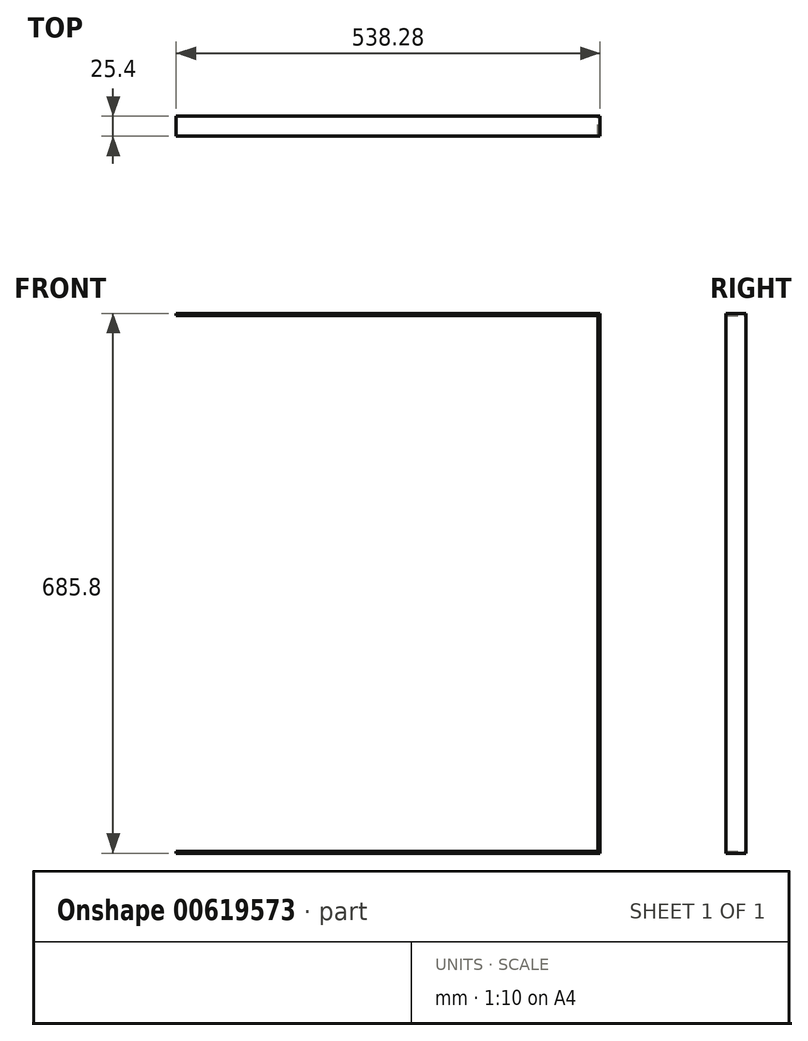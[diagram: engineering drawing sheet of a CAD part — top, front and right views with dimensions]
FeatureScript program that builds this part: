
annotation { "Feature Type Name" : "Feature", "Feature Type Description" : "" }
export const myFeature = defineFeature(function(context is Context, id is Id, definition is map)
    precondition{}
    {
        {
            var Q0;
            Q0=qCreatedBy(makeId("Front.planeOp"),FACE);
            var sketch = newSketch(context, id + "F0", { "sketchPlane" : qUnion([Q0])});
            skLineSegment(sketch, "E0.bottom", {"start": v(-568.3, 468.03) * mm, "end": v(549.3, 468.03) * mm});
            skLineSegment(sketch, "E0.top", {"start": v(-568.3, -217.77) * mm, "end": v(549.3, -217.77) * mm});
            skLineSegment(sketch, "E0.left", {"start": v(-568.3, 468.03) * mm, "end": v(-568.3, -217.77) * mm});
            skLineSegment(sketch, "E0.right", {"start": v(549.3, 468.03) * mm, "end": v(549.3, -217.77) * mm});
            skLineSegment(sketch, "E1", {"start": v(-568.3, 468.03) * mm, "end": v(-555.39, 468.03) * mm});
            skLineSegment(sketch, "E2", {"start": v(-555.39, 468.03) * mm, "end": v(-555.39, -217.77) * mm});
            skLineSegment(sketch, "E3.1.0.0", {"start": v(-4.2, 468.03) * mm, "end": v(-4.2, -217.77) * mm});
            skLineSegment(sketch, "E3.1.0.1", {"start": v(-17.11, 468.03) * mm, "end": v(-4.2, 468.03) * mm});
            skLineSegment(sketch, "E3.1.0.2", {"start": v(-17.11, 468.03) * mm, "end": v(-17.11, -217.77) * mm});
            skLineSegment(sketch, "E3.2.0.0", {"start": v(546.97, 468.03) * mm, "end": v(546.97, -217.77) * mm});
            skLineSegment(sketch, "E3.2.0.1", {"start": v(534.07, 468.03) * mm, "end": v(546.97, 468.03) * mm});
            skLineSegment(sketch, "E3.2.0.2", {"start": v(534.07, 468.03) * mm, "end": v(534.07, -217.77) * mm});
            skLineSegment(sketch, "E3.direction1", {"start": v(-555.39, -217.77) * mm, "end": v(-4.2, -217.77) * mm, "construction": true});
            skSolve(sketch);
        }
        {
            var Q0;
            {var subQ0=sQuery(id+"F0.wireOp",EDGE,"E2");Q0=makeQuery(id+"F0.imprint","IMPRINT",FACE,{"disambiguationData":[TD([[makeQuery(id+"F0.imprint","IMPRINT",EDGE,{"derivedFrom":subQ0}),1.0]])]});}
            extrude(context, id + "F1", {"entities" : qUnion([Q0]), "depth" : 25.4 * mm, "offsetDistance" : 25.4 * mm});
        }
        {
            var Q0;
            Q0=makeQuery(id+"F1.opExtrude","SWEPT_FACE",FACE,{"disambiguationData":[OSD([sQuery(id+"F0.wireOp",EDGE,"E2")])]});
            var Q1;
            Q1=makeQuery(id+"F1.opExtrude","CAP_FACE",FACE,{"disambiguationData":[OSD([sQuery(id+"F0.wireOp",EDGE,"E0.bottom"),sQuery(id+"F0.wireOp",EDGE,"E0.top"),sQuery(id+"F0.wireOp",EDGE,"E2"),sQuery(id+"F0.wireOp",EDGE,"E3.1.0.2")])],"isStart":true});
            var Q2;
            Q2=makeQuery(id+"F1.opExtrude","CAP_FACE",FACE,{"disambiguationData":[OSD([sQuery(id+"F0.wireOp",EDGE,"E0.bottom"),sQuery(id+"F0.wireOp",EDGE,"E0.top"),sQuery(id+"F0.wireOp",EDGE,"E2"),sQuery(id+"F0.wireOp",EDGE,"E3.1.0.2")])],"isStart":false});
            shell(context, id + "F2", {"entities" : qUnion([Q0, Q1, Q2]), "thickness" : 2.54 * mm});
        }
    });
